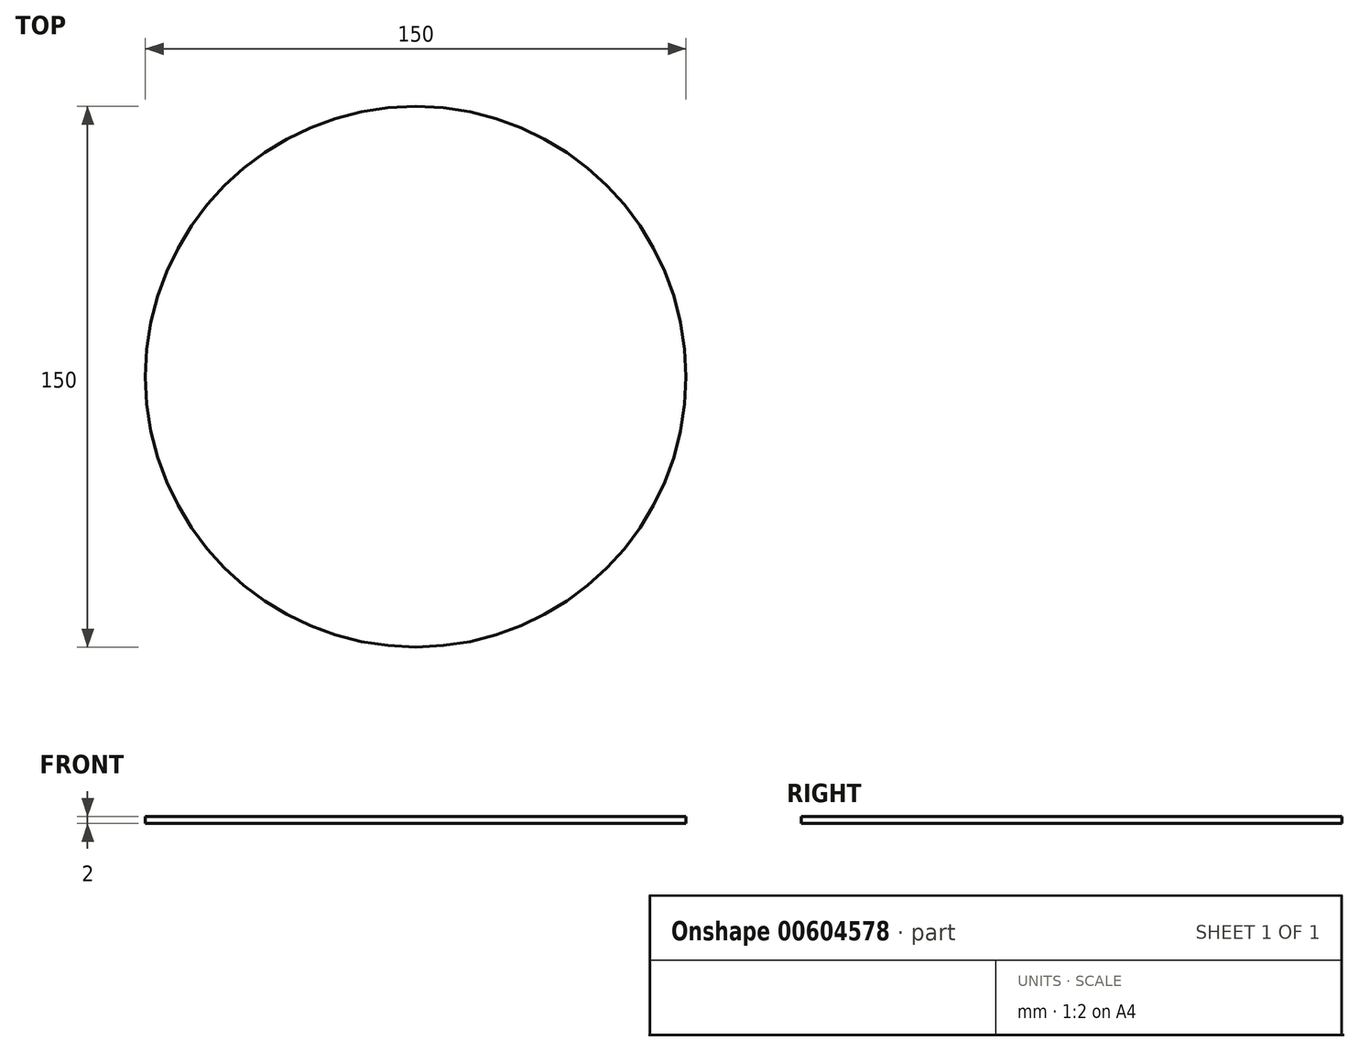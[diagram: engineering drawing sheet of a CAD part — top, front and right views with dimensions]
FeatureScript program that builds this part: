
annotation { "Feature Type Name" : "Feature", "Feature Type Description" : "" }
export const myFeature = defineFeature(function(context is Context, id is Id, definition is map)
    precondition{}
    {
        {
            var Q0;
            Q0=qCreatedBy(makeId("Top.planeOp"),FACE);
            var sketch = newSketch(context, id + "F0", { "sketchPlane" : qUnion([Q0])});
            skCircle(sketch, "E0", {"center": v(0, 0) * mm, "radius": 75 * mm});
            skSolve(sketch);
        }
        {
            var Q0;
            Q0=makeQuery(id+"F0.imprint","IMPRINT",FACE,{"disambiguationData":[TD([[makeQuery(id+"F0.imprint","IMPRINT",EDGE,{"derivedFrom":sQuery(id+"F0.wireOp",EDGE,"E0")}),1.0]])]});
            extrude(context, id + "F1", {"entities" : qUnion([Q0]), "depth" : 2 * mm, "offsetDistance" : 25 * mm});
        }
    });
